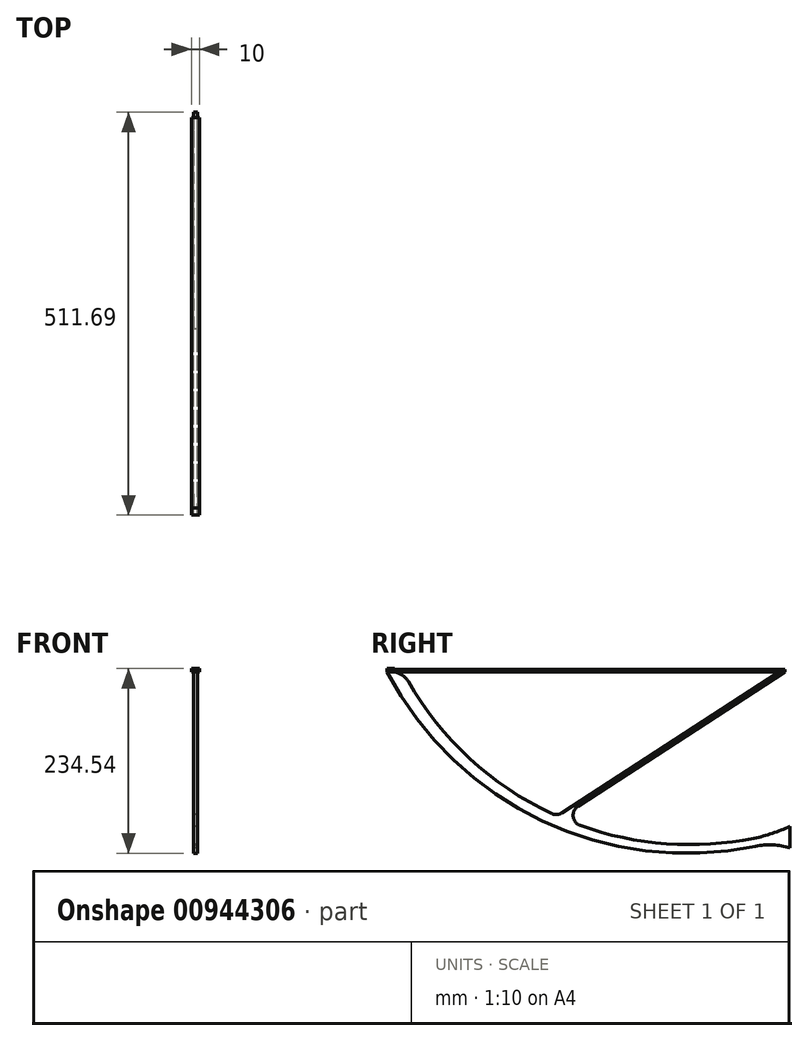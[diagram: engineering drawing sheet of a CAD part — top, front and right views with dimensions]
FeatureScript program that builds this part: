
annotation { "Feature Type Name" : "Feature", "Feature Type Description" : "" }
export const myFeature = defineFeature(function(context is Context, id is Id, definition is map)
    precondition{}
    {
        {
            var Q0;
            Q0=qCreatedBy(makeId("Front.planeOp"),FACE);
            var sketch = newSketch(context, id + "F0", { "sketchPlane" : qUnion([Q0])});
            skLineSegment(sketch, "E0", {"start": v(-5, -10.74) * mm, "end": v(5, -10.74) * mm});
            skLineSegment(sketch, "E1", {"start": v(-5, -7.74) * mm, "end": v(5, -7.74) * mm});
            skLineSegment(sketch, "E2", {"start": v(-5, -7.74) * mm, "end": v(-5, -10.74) * mm});
            skLineSegment(sketch, "E3", {"start": v(5, -7.74) * mm, "end": v(5, -10.74) * mm});
            skSolve(sketch);
        }
        {
            var Q0;
            Q0=makeQuery(id+"F0.imprint","IMPRINT",FACE,{"disambiguationData":[TD([[makeQuery(id+"F0.imprint","IMPRINT",EDGE,{"derivedFrom":sQuery(id+"F0.wireOp",EDGE,"E0")}),1.0]])]});
            var Q1;
            Q1=sQuery(id+"F0.wireOp",EDGE,"E0");
            extrude(context, id + "F1", {"entities" : qUnion([Q0]), "surfaceEntities" : qUnion([Q1]), "depth" : 505 * mm, "offsetDistance" : 25 * mm});
        }
        {
            var Q0;
            Q0=qCreatedBy(makeId("Right.planeOp"),FACE);
            var sketch = newSketch(context, id + "F2", { "sketchPlane" : qUnion([Q0])});
            skLineSegment(sketch, "E4", {"start": v(-505, -10.74) * mm, "end": v(-485, -10.74) * mm});
            skLineSegment(sketch, "E5", {"start": v(-168.85, -115.8) * mm, "end": v(-7.34, -10.74) * mm});
            skLineSegment(sketch, "E6", {"start": v(-164.63, -117.82) * mm, "end": v(0, -10.74) * mm});
            skArc(sketch, "E7.trimOffspring", {"start": v(-168.85, -115.8) * mm, "mid": v(-323.62, -53.33) * mm, "end": v(-485, -10.74) * mm});
            skLineSegment(sketch, "E8", {"start": v(0, -10.74) * mm, "end": v(-7.34, -10.74) * mm});
            skPoint(sketch, "E9.orphan", {"position": v(9.18, 0) * mm});
            skLineSegment(sketch, "E10.direction1", {"start": v(-743.01, -1315.47) * mm, "end": v(-718.01, -1315.47) * mm, "construction": true});
            skArc(sketch, "E11.2.0.0", {"start": v(-129.7, -90.33) * mm, "mid": v(-263.24, -43.25) * mm, "end": v(-401.04, -10.71) * mm});
            skArc(sketch, "E11.2.0.1", {"start": v(-138.89, -96.3) * mm, "mid": v(-278.97, -44.78) * mm, "end": v(-423.96, -9.35) * mm});
            skArc(sketch, "E12.1.0.0", {"start": v(-120.02, -84.03) * mm, "mid": v(-246.18, -40.92) * mm, "end": v(-376.03, -10.71) * mm});
            skArc(sketch, "E12.1.0.1", {"start": v(-129.7, -90.33) * mm, "mid": v(-252.58, -46.23) * mm, "end": v(-379.2, -14.44) * mm});
            skArc(sketch, "E12.2.0.0", {"start": v(-110.9, -78.1) * mm, "mid": v(-219.52, -41.3) * mm, "end": v(-330.92, -14.05) * mm});
            skArc(sketch, "E12.2.0.1", {"start": v(-120.02, -84.03) * mm, "mid": v(-235.48, -43.82) * mm, "end": v(-354.16, -14.42) * mm});
            skArc(sketch, "E13.1.0.0", {"start": v(-110.9, -78.1) * mm, "mid": v(-231.61, -35.14) * mm, "end": v(-355.92, -4.06) * mm});
            skArc(sketch, "E14.trimOffspring", {"start": v(-138.89, -96.3) * mm, "mid": v(-273.7, -46.75) * mm, "end": v(-413.09, -12.08) * mm});
            skArc(sketch, "E15.trimOffspring", {"start": v(-78.28, -56.88) * mm, "mid": v(-137.97, -36.15) * mm, "end": v(-198.57, -18.3) * mm});
            skArc(sketch, "E16.trimOffspring", {"start": v(-69.15, -50.94) * mm, "mid": v(-122.22, -33.15) * mm, "end": v(-176, -17.6) * mm});
            skPoint(sketch, "E17.orphan", {"position": v(-226.82, -11.3) * mm});
            skPoint(sketch, "E18.orphan", {"position": v(-178.25, -10.42) * mm});
            skPoint(sketch, "E19.orphan", {"position": v(-151.7, -10.84) * mm});
            skLineSegment(sketch, "E20", {"start": v(-451, -10.74) * mm, "end": v(-476, -10.74) * mm});
            skLineSegment(sketch, "E21", {"start": v(-423.96, -9.35) * mm, "end": v(-401.04, -10.71) * mm});
            skLineSegment(sketch, "E22", {"start": v(-376.03, -10.71) * mm, "end": v(-330.92, -14.05) * mm});
            skLineSegment(sketch, "E23", {"start": v(-151.7, -10.84) * mm, "end": v(-52.05, -39.82) * mm});
            skLineSegment(sketch, "E24", {"start": v(-178.25, -10.42) * mm, "end": v(-59.8, -44.86) * mm});
            skLineSegment(sketch, "E25.1.0.0", {"start": v(-195.85, -115.8) * mm, "end": v(-191.15, -112.73) * mm});
            skLineSegment(sketch, "E25.1.0.1", {"start": v(-191.63, -117.82) * mm, "end": v(-188.52, -115.8) * mm});
            skLineSegment(sketch, "E25.2.0.0", {"start": v(-200.4, -101.2) * mm, "end": v(-171.87, -82.63) * mm});
            skLineSegment(sketch, "E25.2.0.1", {"start": v(-196.07, -103.14) * mm, "end": v(-167.33, -84.45) * mm});
            skLineSegment(sketch, "E25.3.0.0", {"start": v(-216.53, -94.12) * mm, "end": v(-188.73, -76.04) * mm});
            skLineSegment(sketch, "E25.3.0.1", {"start": v(-212.12, -96.02) * mm, "end": v(-184.12, -77.81) * mm});
            skLineSegment(sketch, "E25.4.0.0", {"start": v(-232.89, -87.2) * mm, "end": v(-205.85, -69.61) * mm});
            skLineSegment(sketch, "E25.4.0.1", {"start": v(-228.42, -89.06) * mm, "end": v(-201.18, -71.34) * mm});
            skLineSegment(sketch, "E25.5.0.0", {"start": v(-249.49, -80.43) * mm, "end": v(-223.24, -63.36) * mm});
            skLineSegment(sketch, "E25.5.0.1", {"start": v(-244.95, -82.25) * mm, "end": v(-218.5, -65.04) * mm});
            skLineSegment(sketch, "E25.6.0.0", {"start": v(-266.34, -73.83) * mm, "end": v(-240.9, -57.3) * mm});
            skLineSegment(sketch, "E25.6.0.1", {"start": v(-261.73, -75.6) * mm, "end": v(-236.08, -58.92) * mm});
            skLineSegment(sketch, "E25.7.0.0", {"start": v(-283.45, -67.4) * mm, "end": v(-258.86, -51.4) * mm});
            skLineSegment(sketch, "E25.7.0.1", {"start": v(-278.77, -69.13) * mm, "end": v(-253.95, -52.98) * mm});
            skLineSegment(sketch, "E25.8.0.0", {"start": v(-300.82, -61.14) * mm, "end": v(-277.1, -45.7) * mm});
            skLineSegment(sketch, "E25.8.0.1", {"start": v(-296.07, -62.82) * mm, "end": v(-272.12, -47.24) * mm});
            skLineSegment(sketch, "E25.9.0.0", {"start": v(-318.47, -55.05) * mm, "end": v(-295.65, -40.21) * mm});
            skLineSegment(sketch, "E25.9.0.1", {"start": v(-313.64, -56.69) * mm, "end": v(-290.58, -41.69) * mm});
            skLineSegment(sketch, "E25.10.0.0", {"start": v(-336.4, -49.15) * mm, "end": v(-314.52, -34.92) * mm});
            skLineSegment(sketch, "E25.10.0.1", {"start": v(-331.5, -50.74) * mm, "end": v(-309.36, -36.34) * mm});
            skLineSegment(sketch, "E25.11.0.0", {"start": v(-354.62, -43.45) * mm, "end": v(-333.72, -29.85) * mm});
            skLineSegment(sketch, "E25.11.0.1", {"start": v(-349.64, -44.98) * mm, "end": v(-328.47, -31.2) * mm});
            skLineSegment(sketch, "E25.12.0.0", {"start": v(-373.15, -37.94) * mm, "end": v(-353.26, -25) * mm});
            skLineSegment(sketch, "E25.12.0.1", {"start": v(-368.09, -39.41) * mm, "end": v(-347.92, -26.3) * mm});
            skLineSegment(sketch, "E25.13.0.0", {"start": v(-392, -32.63) * mm, "end": v(-373.16, -20.38) * mm});
            skLineSegment(sketch, "E25.13.0.1", {"start": v(-386.84, -34.05) * mm, "end": v(-367.72, -21.61) * mm});
            skLineSegment(sketch, "E25.14.0.0", {"start": v(-411.16, -27.54) * mm, "end": v(-393.43, -16) * mm});
            skLineSegment(sketch, "E25.14.0.1", {"start": v(-405.92, -28.9) * mm, "end": v(-387.89, -17.17) * mm});
            skLineSegment(sketch, "E25.15.0.0", {"start": v(-430.68, -22.67) * mm, "end": v(-414.1, -11.89) * mm});
            skLineSegment(sketch, "E25.15.0.1", {"start": v(-425.34, -23.97) * mm, "end": v(-408.45, -12.98) * mm});
            skLineSegment(sketch, "E25.16.0.0", {"start": v(-450.54, -18.03) * mm, "end": v(-439.34, -10.74) * mm});
            skLineSegment(sketch, "E25.16.0.1", {"start": v(-445.1, -19.27) * mm, "end": v(-432, -10.74) * mm});
            skLineSegment(sketch, "E25.direction1", {"start": v(-168.85, -115.8) * mm, "end": v(-195.85, -115.8) * mm, "construction": true});
            skLineSegment(sketch, "E26.trimOffspring", {"start": v(-184.52, -108.42) * mm, "end": v(-155.26, -89.39) * mm});
            skLineSegment(sketch, "E27.trimOffspring", {"start": v(-180.24, -110.4) * mm, "end": v(-150.78, -91.25) * mm});
            skLineSegment(sketch, "E28.trimOffspring", {"start": v(-233.2, -52.28) * mm, "end": v(-225.04, -46.97) * mm});
            skLineSegment(sketch, "E29.trimOffspring", {"start": v(-228.3, -53.86) * mm, "end": v(-220.06, -48.5) * mm});
            skLineSegment(sketch, "E30.trimOffspring", {"start": v(-215.27, -58.18) * mm, "end": v(-206.83, -52.69) * mm});
            skLineSegment(sketch, "E31.trimOffspring", {"start": v(-210.45, -59.81) * mm, "end": v(-201.94, -54.28) * mm});
            skLineSegment(sketch, "E32.trimOffspring", {"start": v(-197.62, -64.26) * mm, "end": v(-188.92, -58.6) * mm});
            skLineSegment(sketch, "E33.trimOffspring", {"start": v(-192.88, -65.94) * mm, "end": v(-184.1, -60.24) * mm});
            skLineSegment(sketch, "E34.trimOffspring", {"start": v(-180.25, -70.52) * mm, "end": v(-171.3, -64.7) * mm});
            skLineSegment(sketch, "E35.trimOffspring", {"start": v(-175.58, -72.25) * mm, "end": v(-166.55, -66.38) * mm});
            skLineSegment(sketch, "E36.trimOffspring", {"start": v(-158.54, -78.73) * mm, "end": v(-149.27, -72.7) * mm});
            skLineSegment(sketch, "E37.trimOffspring", {"start": v(-163.14, -76.96) * mm, "end": v(-153.94, -70.97) * mm});
            skLineSegment(sketch, "E38.trimOffspring", {"start": v(-146.3, -83.56) * mm, "end": v(-136.85, -77.42) * mm});
            skLineSegment(sketch, "E39.trimOffspring", {"start": v(-141.76, -85.38) * mm, "end": v(-132.25, -79.2) * mm});
            skLineSegment(sketch, "E40.trimOffspring", {"start": v(-251.43, -46.57) * mm, "end": v(-243.55, -41.45) * mm});
            skLineSegment(sketch, "E41.trimOffspring", {"start": v(-246.45, -48.1) * mm, "end": v(-238.49, -42.93) * mm});
            skLineSegment(sketch, "E42.trimOffspring", {"start": v(-269.97, -41.07) * mm, "end": v(-262.37, -36.13) * mm});
            skLineSegment(sketch, "E43.trimOffspring", {"start": v(-264.9, -42.54) * mm, "end": v(-257.22, -37.55) * mm});
            skLineSegment(sketch, "E44.trimOffspring", {"start": v(-288.81, -35.77) * mm, "end": v(-281.53, -31.03) * mm});
            skLineSegment(sketch, "E45.trimOffspring", {"start": v(-283.66, -37.19) * mm, "end": v(-276.29, -32.4) * mm});
            skLineSegment(sketch, "E46.trimOffspring", {"start": v(-308, -30.68) * mm, "end": v(-301.02, -26.15) * mm});
            skLineSegment(sketch, "E47.trimOffspring", {"start": v(-302.75, -32.04) * mm, "end": v(-295.7, -27.45) * mm});
            skLineSegment(sketch, "E48.trimOffspring", {"start": v(-327.52, -25.82) * mm, "end": v(-320.88, -21.5) * mm});
            skLineSegment(sketch, "E49.trimOffspring", {"start": v(-322.18, -27.11) * mm, "end": v(-315.44, -22.74) * mm});
            skLineSegment(sketch, "E50.trimOffspring", {"start": v(-347.4, -21.18) * mm, "end": v(-341.1, -17.1) * mm});
            skLineSegment(sketch, "E51.trimOffspring", {"start": v(-341.96, -22.42) * mm, "end": v(-335.57, -18.26) * mm});
            skLineSegment(sketch, "E52.trimOffspring", {"start": v(-367.65, -16.8) * mm, "end": v(-361.72, -12.94) * mm});
            skLineSegment(sketch, "E53.trimOffspring", {"start": v(-362.1, -17.96) * mm, "end": v(-356.08, -14.04) * mm});
            skLineSegment(sketch, "E54.trimOffspring", {"start": v(-388.3, -12.66) * mm, "end": v(-385.34, -10.74) * mm});
            skLineSegment(sketch, "E55.trimOffspring", {"start": v(-382.65, -13.76) * mm, "end": v(-378, -10.74) * mm});
            skPoint(sketch, "E56.orphan", {"position": v(-405, -10.74) * mm});
            skPoint(sketch, "E57.orphan", {"position": v(-412.34, -10.74) * mm});
            skLineSegment(sketch, "E58.trimOffspring", {"start": v(-127.94, -71.62) * mm, "end": v(-95.55, -50.55) * mm});
            skLineSegment(sketch, "E59.trimOffspring", {"start": v(-123.28, -73.36) * mm, "end": v(-90.83, -52.26) * mm});
            skLineSegment(sketch, "E60.trimOffspring", {"start": v(-145.25, -65.32) * mm, "end": v(-113.1, -44.4) * mm});
            skLineSegment(sketch, "E61.trimOffspring", {"start": v(-140.52, -67.01) * mm, "end": v(-108.3, -46.06) * mm});
            skLineSegment(sketch, "E62.trimOffspring", {"start": v(-162.83, -59.2) * mm, "end": v(-130.92, -38.44) * mm});
            skLineSegment(sketch, "E63.trimOffspring", {"start": v(-158.03, -60.84) * mm, "end": v(-126.05, -40.04) * mm});
            skLineSegment(sketch, "E64.trimOffspring", {"start": v(-180.7, -53.25) * mm, "end": v(-149.03, -32.66) * mm});
            skLineSegment(sketch, "E65.trimOffspring", {"start": v(-175.82, -54.85) * mm, "end": v(-144.08, -34.2) * mm});
            skLineSegment(sketch, "E66.trimOffspring", {"start": v(-198.86, -47.5) * mm, "end": v(-167.45, -27.07) * mm});
            skLineSegment(sketch, "E67.trimOffspring", {"start": v(-193.9, -49.04) * mm, "end": v(-162.42, -28.57) * mm});
            skLineSegment(sketch, "E68.trimOffspring", {"start": v(-217.32, -41.95) * mm, "end": v(-186.18, -21.7) * mm});
            skLineSegment(sketch, "E69.trimOffspring", {"start": v(-212.27, -43.44) * mm, "end": v(-181.06, -23.14) * mm});
            skLineSegment(sketch, "E70.trimOffspring", {"start": v(-236.1, -36.6) * mm, "end": v(-205.23, -16.53) * mm});
            skLineSegment(sketch, "E71.trimOffspring", {"start": v(-230.96, -38.03) * mm, "end": v(-200.02, -17.9) * mm});
            skLineSegment(sketch, "E72.trimOffspring", {"start": v(-255.2, -31.46) * mm, "end": v(-224.62, -11.58) * mm});
            skLineSegment(sketch, "E73.trimOffspring", {"start": v(-249.97, -32.83) * mm, "end": v(-219.32, -12.9) * mm});
            skLineSegment(sketch, "E74.trimOffspring", {"start": v(-274.63, -26.54) * mm, "end": v(-250.34, -10.74) * mm});
            skLineSegment(sketch, "E75.trimOffspring", {"start": v(-269.31, -27.85) * mm, "end": v(-243, -10.74) * mm});
            skLineSegment(sketch, "E76.trimOffspring", {"start": v(-294.43, -21.85) * mm, "end": v(-277.34, -10.74) * mm});
            skLineSegment(sketch, "E77.trimOffspring", {"start": v(-289.01, -23.1) * mm, "end": v(-270, -10.74) * mm});
            skLineSegment(sketch, "E78.trimOffspring", {"start": v(-314.6, -17.4) * mm, "end": v(-304.34, -10.74) * mm});
            skLineSegment(sketch, "E79.trimOffspring", {"start": v(-309.07, -18.6) * mm, "end": v(-297, -10.74) * mm});
            skPoint(sketch, "E80.orphan", {"position": v(-358.34, -10.74) * mm});
            skPoint(sketch, "E81.orphan", {"position": v(-351, -10.74) * mm});
            skLineSegment(sketch, "E82.trimOffspring", {"start": v(-335.14, -13.22) * mm, "end": v(-331.34, -10.74) * mm});
            skLineSegment(sketch, "E83.trimOffspring", {"start": v(-329.52, -14.33) * mm, "end": v(-324, -10.74) * mm});
            skLineSegment(sketch, "E84.trimOffspring", {"start": v(-86.69, -44.79) * mm, "end": v(-78.46, -39.44) * mm});
            skLineSegment(sketch, "E85.trimOffspring", {"start": v(-81.9, -46.44) * mm, "end": v(-73.39, -40.91) * mm});
            skLineSegment(sketch, "E86.trimOffspring", {"start": v(-104.5, -38.81) * mm, "end": v(-97.12, -34.01) * mm});
            skLineSegment(sketch, "E87.trimOffspring", {"start": v(-99.63, -40.42) * mm, "end": v(-92.05, -35.49) * mm});
            skLineSegment(sketch, "E88.trimOffspring", {"start": v(-141, -27.44) * mm, "end": v(-134.43, -23.16) * mm});
            skLineSegment(sketch, "E89.trimOffspring", {"start": v(-135.98, -28.94) * mm, "end": v(-129.36, -24.63) * mm});
            skLineSegment(sketch, "E90.trimOffspring", {"start": v(-122.6, -33.03) * mm, "end": v(-115.78, -28.59) * mm});
            skLineSegment(sketch, "E91.trimOffspring", {"start": v(-117.65, -34.58) * mm, "end": v(-110.7, -30.06) * mm});
            skLineSegment(sketch, "E92.trimOffspring", {"start": v(-159.72, -22.05) * mm, "end": v(-153.1, -17.74) * mm});
            skLineSegment(sketch, "E93.trimOffspring", {"start": v(-154.6, -23.5) * mm, "end": v(-148.02, -19.2) * mm});
            skLineSegment(sketch, "E94.trimOffspring", {"start": v(-178.76, -16.87) * mm, "end": v(-171.75, -12.3) * mm});
            skLineSegment(sketch, "E95.trimOffspring", {"start": v(-173.56, -18.26) * mm, "end": v(-166.68, -13.78) * mm});
            skLineSegment(sketch, "E96.trimOffspring", {"start": v(-198.14, -11.91) * mm, "end": v(-196.34, -10.74) * mm});
            skLineSegment(sketch, "E97.trimOffspring", {"start": v(-192.84, -13.24) * mm, "end": v(-189, -10.74) * mm});
            skLineSegment(sketch, "E98.trimOffspring", {"start": v(-70.7, -34.4) * mm, "end": v(-34.34, -10.74) * mm});
            skLineSegment(sketch, "E99.trimOffspring", {"start": v(-65.64, -35.87) * mm, "end": v(-27, -10.74) * mm});
            skLineSegment(sketch, "E100.trimOffspring", {"start": v(-89.37, -28.97) * mm, "end": v(-61.34, -10.74) * mm});
            skLineSegment(sketch, "E101.trimOffspring", {"start": v(-84.3, -30.44) * mm, "end": v(-54, -10.74) * mm});
            skLineSegment(sketch, "E102.trimOffspring", {"start": v(-108.02, -23.54) * mm, "end": v(-88.34, -10.74) * mm});
            skLineSegment(sketch, "E103.trimOffspring", {"start": v(-102.95, -25.02) * mm, "end": v(-81, -10.74) * mm});
            skLineSegment(sketch, "E104.trimOffspring", {"start": v(-126.68, -18.12) * mm, "end": v(-115.34, -10.74) * mm});
            skLineSegment(sketch, "E105.trimOffspring", {"start": v(-121.61, -19.6) * mm, "end": v(-108, -10.74) * mm});
            skLineSegment(sketch, "E106.trimOffspring", {"start": v(-145.34, -12.7) * mm, "end": v(-142.34, -10.74) * mm});
            skLineSegment(sketch, "E107.trimOffspring", {"start": v(-140.27, -14.17) * mm, "end": v(-135, -10.74) * mm});
            skLineSegment(sketch, "E108", {"start": v(-176, -17.6) * mm, "end": v(-178.2, -17.02) * mm});
            skLineSegment(sketch, "E109", {"start": v(-198.57, -18.3) * mm, "end": v(-200.92, -17.67) * mm});
            skPoint(sketch, "E110", {"position": v(-200.92, -17.67) * mm});
            skLineSegment(sketch, "E111", {"start": v(-178.2, -17.02) * mm, "end": v(-175.94, -17.67) * mm});
            skLineSegment(sketch, "E112", {"start": v(-176.99, -17.37) * mm, "end": v(-175.94, -17.67) * mm});
            skLineSegment(sketch, "E113", {"start": v(-200.92, -17.67) * mm, "end": v(-243, -10.74) * mm});
            skLineSegment(sketch, "E114", {"start": v(-243, -10.74) * mm, "end": v(-250.34, -10.74) * mm});
            skLineSegment(sketch, "E115", {"start": v(-270, -10.74) * mm, "end": v(-250.34, -10.74) * mm});
            skLineSegment(sketch, "E116", {"start": v(-297, -10.74) * mm, "end": v(-277.34, -10.74) * mm});
            skLineSegment(sketch, "E117", {"start": v(-270, -10.74) * mm, "end": v(-277.34, -10.74) * mm});
            skLineSegment(sketch, "E118", {"start": v(-324, -10.74) * mm, "end": v(-304.34, -10.74) * mm});
            skLineSegment(sketch, "E119", {"start": v(-324, -10.74) * mm, "end": v(-330.92, -14.05) * mm});
            skLineSegment(sketch, "E120", {"start": v(-376.03, -10.71) * mm, "end": v(-378, -10.74) * mm});
            skLineSegment(sketch, "E121", {"start": v(-385.34, -10.74) * mm, "end": v(-379.2, -14.44) * mm});
            skLineSegment(sketch, "E122", {"start": v(-385.34, -10.74) * mm, "end": v(-378, -10.74) * mm});
            skLineSegment(sketch, "E123", {"start": v(-423.96, -9.35) * mm, "end": v(-432, -10.74) * mm});
            skLineSegment(sketch, "E124", {"start": v(-441.95, -10.8) * mm, "end": v(-485, -10.74) * mm});
            skLineSegment(sketch, "E125", {"start": v(-304.34, -10.74) * mm, "end": v(-297, -10.74) * mm});
            skPoint(sketch, "E126", {"position": v(-176.99, -17.37) * mm});
            skLineSegment(sketch, "E127", {"start": v(-175.94, -17.67) * mm, "end": v(-200.92, -17.67) * mm});
            skPoint(sketch, "E128", {"position": v(-153.82, -10.24) * mm});
            skLineSegment(sketch, "E129", {"start": v(-153.82, -10.24) * mm, "end": v(-178.54, -6.56) * mm});
            skLineSegment(sketch, "E130", {"start": v(-151.7, -10.84) * mm, "end": v(-153.73, -10.25) * mm});
            skLineSegment(sketch, "E131", {"start": v(-178.25, -10.42) * mm, "end": v(-180.27, -9.83) * mm});
            skPoint(sketch, "E132", {"position": v(-180.27, -9.83) * mm});
            skLineSegment(sketch, "E133", {"start": v(-180.27, -9.83) * mm, "end": v(-156.56, -9.83) * mm});
            skLineSegment(sketch, "E134", {"start": v(-180.27, -9.83) * mm, "end": v(-178.2, -17.02) * mm});
            skLineSegment(sketch, "E135", {"start": v(-7.34, -10.74) * mm, "end": v(-153.82, -10.24) * mm});
            skArc(sketch, "E136", {"start": v(-505, -10.74) * mm, "mid": v(-295.87, -205.45) * mm, "end": v(-10.88, -226.13) * mm});
            skArc(sketch, "E137", {"start": v(-485, -10.74) * mm, "mid": v(-283.95, -196.5) * mm, "end": v(-10.88, -215.53) * mm});
            skLineSegment(sketch, "E138", {"start": v(-10.88, -215.53) * mm, "end": v(-10.88, -226.13) * mm});
            skLineSegment(sketch, "E139", {"start": v(-7.34, -10.74) * mm, "end": v(-289.32, -194.14) * mm});
            skLineSegment(sketch, "E140", {"start": v(0, -10.74) * mm, "end": v(-289.32, -198.91) * mm});
            skArc(sketch, "E141.trimOffspring", {"start": v(-175.6, -120.18) * mm, "mid": v(-336.68, -54.58) * mm, "end": v(-505, -10.74) * mm});
            skPoint(sketch, "E142.orphan", {"position": v(0, -223) * mm});
            skLineSegment(sketch, "E143", {"start": v(-10.88, -215.53) * mm, "end": v(6.69, -207.1) * mm});
            skLineSegment(sketch, "E144", {"start": v(-10.88, -226.13) * mm, "end": v(6.69, -234.57) * mm});
            skLineSegment(sketch, "E145", {"start": v(6.69, -234.57) * mm, "end": v(6.69, -207.1) * mm});
            skSolve(sketch);
        }
        {
            var Q0;
            {var subQ0=sQuery(id+"F2.wireOp",EDGE,"E4");Q0=makeQuery(id+"F2.imprint","IMPRINT",FACE,{"disambiguationData":[TD([[makeQuery(id+"F2.imprint","IMPRINT",EDGE,{"derivedFrom":subQ0}),-1.0]])]});}
            var Q1;
            {var subQ5=sQuery(id+"F2.wireOp",EDGE,"E138");Q1=makeQuery(id+"F2.imprint","IMPRINT",FACE,{"disambiguationData":[TD([[makeQuery(id+"F2.imprint","IMPRINT",EDGE,{"derivedFrom":subQ5}),-1.0]])]});}
            var Q2;
            {var subQ8=sQuery(id+"F2.wireOp",EDGE,"E8");Q2=makeQuery(id+"F2.imprint","IMPRINT",FACE,{"disambiguationData":[TD([[makeQuery(id+"F2.imprint","IMPRINT",EDGE,{"derivedFrom":subQ8}),1.0]])]});}
            var Q3;
            Q3=makeQuery(id+"F2.imprint","IMPRINT",FACE,{"disambiguationData":[TD([[makeQuery(id+"F2.imprint","IMPRINT",EDGE,{"derivedFrom":sQuery(id+"F2.wireOp",EDGE,"E138")}),1.0]])]});
            extrude(context, id + "F3", {"entities" : qUnion([Q0, Q1, Q2, Q3]), "endBound" : BoundingType.SYMMETRIC, "depth" : 5 * mm, "offsetDistance" : 25 * mm});
        }
        {
            var Q0;
            Q0=makeQuery(id+"F1.opExtrude","SWEPT_FACE",FACE,{"disambiguationData":[OSD([sQuery(id+"F0.wireOp",EDGE,"E1")])]});
            var sketch = newSketch(context, id + "F4", { "sketchPlane" : qUnion([Q0])});
            skLineSegment(sketch, "E146.bottom", {"start": v(-5, -495.61) * mm, "end": v(5, -495.61) * mm});
            skLineSegment(sketch, "E146.top", {"start": v(-5, -505) * mm, "end": v(5, -505) * mm});
            skLineSegment(sketch, "E146.left", {"start": v(-5, -495.61) * mm, "end": v(-5, -505) * mm});
            skLineSegment(sketch, "E146.right", {"start": v(5, -495.61) * mm, "end": v(5, -505) * mm});
            skSolve(sketch);
        }
        {
            var Q0;
            Q0=makeQuery(id+"F4.imprint","IMPRINT",FACE,{"disambiguationData":[TD([[makeQuery(id+"F4.imprint","IMPRINT",EDGE,{"derivedFrom":sQuery(id+"F4.wireOp",EDGE,"E146.bottom")}),-1.0]])]});
            extrude(context, id + "F5", {"entities" : qUnion([Q0]), "operationType" : NewBodyOperationType.ADD, "depth" : 1 * mm, "offsetDistance" : 25 * mm});
        }
        {
            var Q0;
            {var subQ0=sQuery(id+"F2.wireOp",EDGE,"E137");var subQ1=sQuery(id+"F2.wireOp",EDGE,"m8f4QzZn-tKJH-lgp6-LZa1-5HskhMRDKc9X");Q0=makeQuery(id+"F3.opExtrude","SWEPT_EDGE",EDGE,{"disambiguationData":[OSD([subQ1,subQ0]),TDD([makeQuery(id+"F2.imprint","INTERSECT",VERTEX,{"disambiguationData":[OD(0.0)],"derivedFrom":[subQ1,subQ0]})])]});}
            fillet(context, id + "F6", {"entities" : qUnion([Q0]), "radius" : 13.86 * mm, "tangentPropagation" : true, "allowEdgeOverflow" : false});
        }
        {
            var Q0;
            Q0=makeQuery(id+"F3.opExtrude","SWEPT_EDGE",EDGE,{"disambiguationData":[OSD([sQuery(id+"F2.wireOp",EDGE,"E7.trimOffspring"),sQuery(id+"F2.wireOp",EDGE,"E20"),sQuery(id+"F2.wireOp",EDGE,"E124"),sQuery(id+"F2.wireOp",EDGE,"E137")])]});
            fillet(context, id + "F7", {"entities" : qUnion([Q0]), "radius" : 24.5 * mm, "tangentPropagation" : true, "allowEdgeOverflow" : false});
        }
        {
            var Q0;
            Q0=makeQuery(id+"F3.opExtrude","SWEPT_EDGE",EDGE,{"disambiguationData":[OSD([sQuery(id+"F2.wireOp",EDGE,"E137"),sQuery(id+"F2.wireOp",EDGE,"E138"),sQuery(id+"F2.wireOp",EDGE,"E143")])]});
            fillet(context, id + "F8", {"entities" : qUnion([Q0]), "radius" : 198.8 * mm, "tangentPropagation" : true, "allowEdgeOverflow" : false});
        }
        {
            var Q0;
            Q0=makeQuery(id+"F3.opExtrude","SWEPT_EDGE",EDGE,{"disambiguationData":[OSD([sQuery(id+"F2.wireOp",EDGE,"E136"),sQuery(id+"F2.wireOp",EDGE,"E138"),sQuery(id+"F2.wireOp",EDGE,"E144")])]});
            fillet(context, id + "F9", {"entities" : qUnion([Q0]), "radius" : 87.69 * mm, "tangentPropagation" : true, "allowEdgeOverflow" : false});
        }
        {
            var Q0;
            Q0=makeQuery(id+"F3.opExtrude","SWEPT_EDGE",EDGE,{"disambiguationData":[OSD([sQuery(id+"F2.wireOp",EDGE,"E8"),sQuery(id+"F2.wireOp",EDGE,"E135"),sQuery(id+"F2.wireOp",EDGE,"E139")])]});
            fillet(context, id + "F10", {"entities" : qUnion([Q0]), "radius" : 3.93 * mm, "tangentPropagation" : true, "allowEdgeOverflow" : false});
        }
    });
